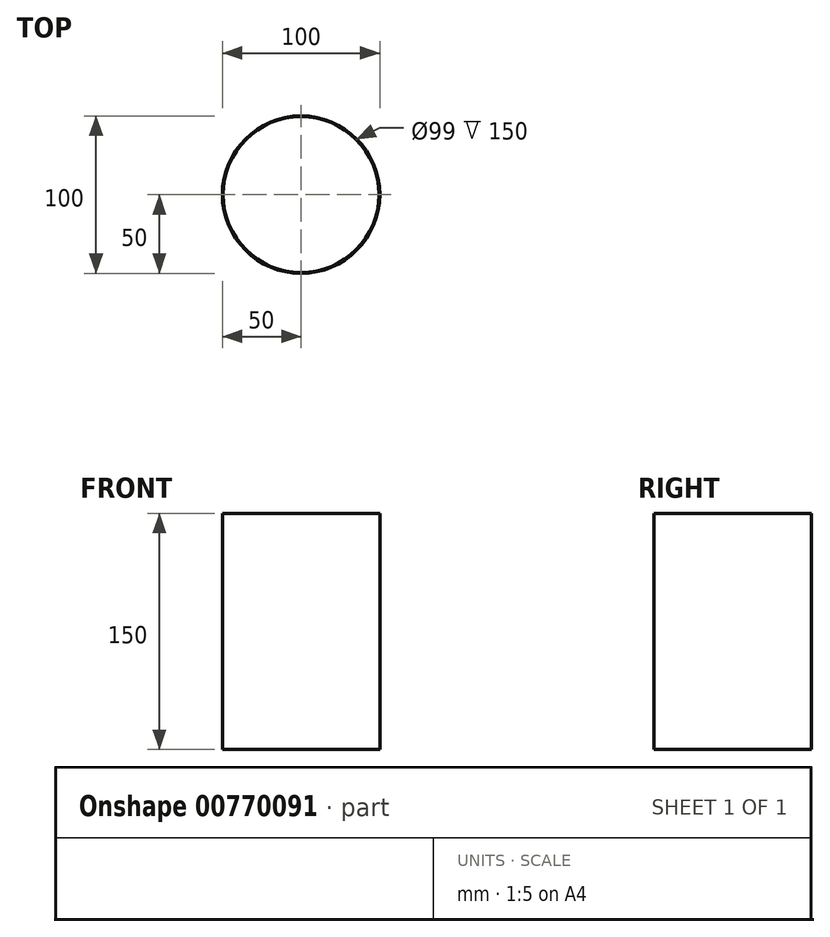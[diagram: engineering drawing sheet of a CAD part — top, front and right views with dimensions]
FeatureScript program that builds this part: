
annotation { "Feature Type Name" : "Feature", "Feature Type Description" : "" }
export const myFeature = defineFeature(function(context is Context, id is Id, definition is map)
    precondition{}
    {
        {
            var Q0;
            Q0=qCreatedBy(makeId("Top.planeOp"),FACE);
            var sketch = newSketch(context, id + "F0", { "sketchPlane" : qUnion([Q0])});
            skCircle(sketch, "E0", {"center": v(0, 0) * mm, "radius": 50 * mm});
            skCircle(sketch, "E1", {"center": v(0, 0) * mm, "radius": 49.5 * mm});
            skSolve(sketch);
        }
        {
            var Q0;
            Q0=makeQuery(id+"F0.imprint","IMPRINT",FACE,{"disambiguationData":[TD([[makeQuery(id+"F0.imprint","IMPRINT",EDGE,{"derivedFrom":sQuery(id+"F0.wireOp",EDGE,"E0")}),1.0]])]});
            extrude(context, id + "F1", {"entities" : qUnion([Q0]), "depth" : 150 * mm, "offsetDistance" : 25 * mm});
        }
    });
